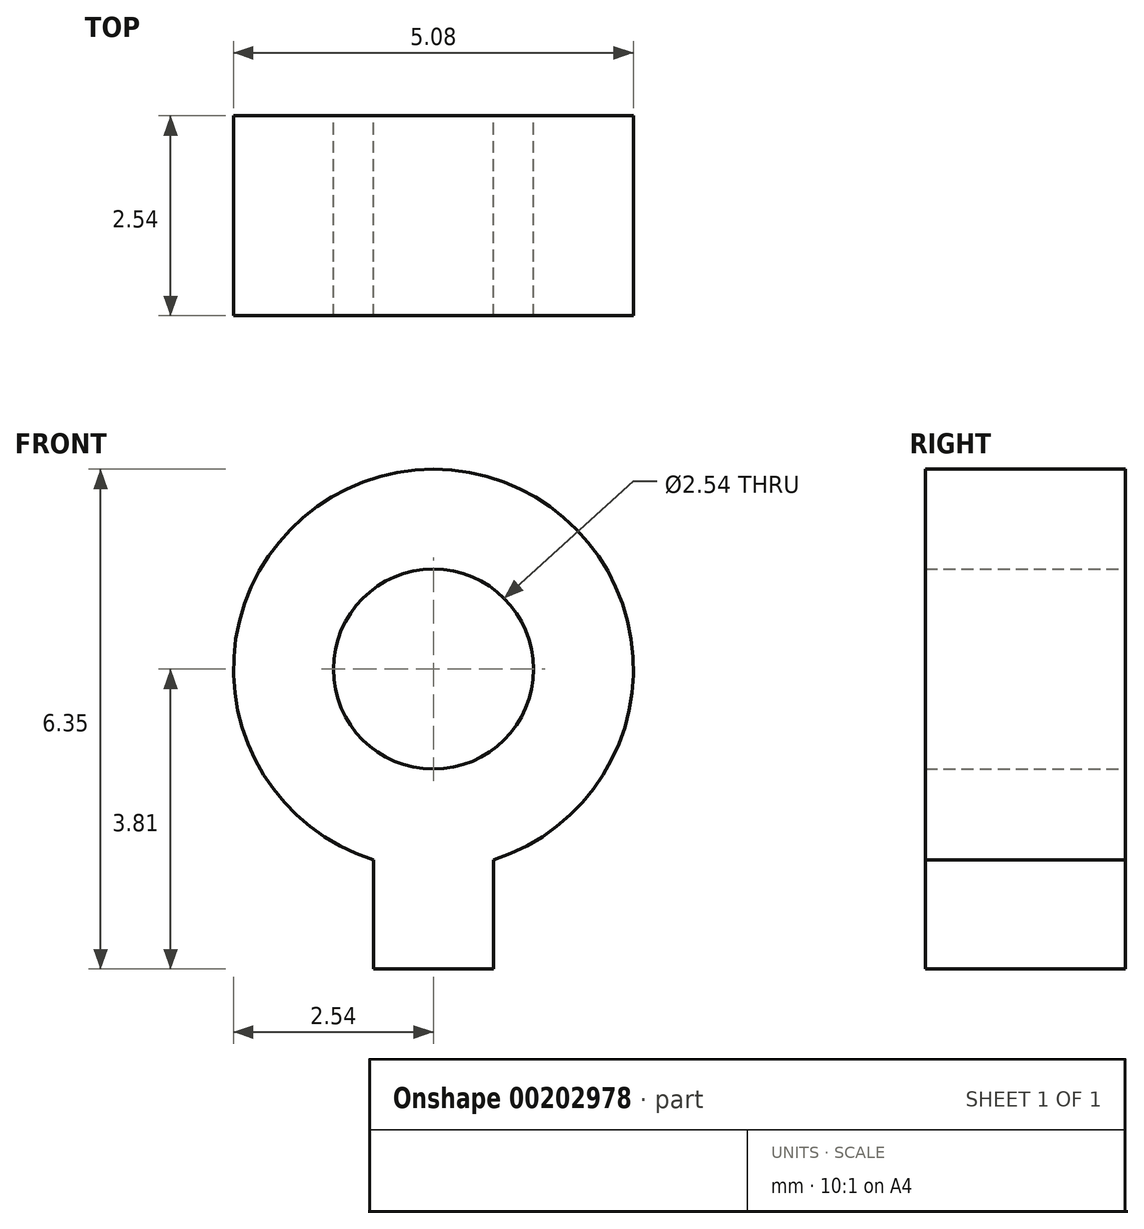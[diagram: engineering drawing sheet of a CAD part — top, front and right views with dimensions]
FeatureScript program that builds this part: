
annotation { "Feature Type Name" : "Feature", "Feature Type Description" : "" }
export const myFeature = defineFeature(function(context is Context, id is Id, definition is map)
    precondition{}
    {
        {
            var Q0;
            Q0=qCreatedBy(makeId("Front.planeOp"),FACE);
            var sketch = newSketch(context, id + "F0", { "sketchPlane" : qUnion([Q0])});
            skCircle(sketch, "E0", {"center": v(0, 0) * mm, "radius": 1.27 * mm});
            skArc(sketch, "E1", {"start": v(0.76, -2.42) * mm, "mid": v(0, 2.54) * mm, "end": v(-0.76, -2.42) * mm});
            skLineSegment(sketch, "E2.0", {"start": v(-0.76, -3.81) * mm, "end": v(0.76, -3.81) * mm});
            skLineSegment(sketch, "E3.trimOffspring", {"start": v(0.76, -2.42) * mm, "end": v(0.76, -3.81) * mm});
            skLineSegment(sketch, "E4.trimOffspring", {"start": v(-0.76, -2.42) * mm, "end": v(-0.76, -3.81) * mm});
            skPoint(sketch, "E5.orphan", {"position": v(-2.54, 0) * mm});
            skPoint(sketch, "E6.start.orphan", {"position": v(0, 2.54) * mm});
            skSolve(sketch);
        }
        {
            var Q0;
            Q0=makeQuery(id+"F0.imprint","IMPRINT",FACE,{"disambiguationData":[TD([[makeQuery(id+"F0.imprint","IMPRINT",EDGE,{"derivedFrom":sQuery(id+"F0.wireOp",EDGE,"E0")}),-1.0]])]});
            extrude(context, id + "F1", {"entities" : qUnion([Q0]), "depth" : 2.54 * mm});
        }
    });
